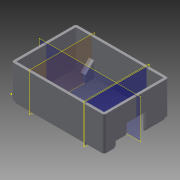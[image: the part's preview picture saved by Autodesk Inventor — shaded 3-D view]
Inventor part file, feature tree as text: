
AUTODESK INVENTOR PART (.ipt)
format: ipt  version: 2015 (Build 190159000, 159)  size: 256,512 bytes
history: native  units: in
note: dims shown in document units (in); Inventor stores cm internally (conversion verified against a paired STEP export)
features: sketch x10, extrude x5, plane x4, fillet x3, rib x3, hole x1, mirror x1
ambient origin geometry x8: Origin, YZ Plane, XZ Plane, XY Plane, X Axis, Y Axis, Z Axis, Center Point
bodies: Solid1 (feature_tree)
feature tree (27):
  extrude  "Extrusion1"  Depth=2.5197in
  extrude  "Extrusion2"  Depth=0.0984in
  fillet  "Fillet1"  Radius=0.0984in
  sketch  "Sketch4"  dims[d7=0.0984in d8=1.2795in d9=0.0in]
  extrude  "Extrusion4"  Depth=1.2795in TaperAngle=0.0deg
  extrude  "Extrusion5"  Depth=0.0787in
  hole  "Hole1"  [1 undecoded]
  extrude  "Extrusion6"  Depth=0.3346in
  fillet  "Fillet2"  [1 undecoded]
  sketch  "Sketch10"  dims[d26=0.3346in]
  plane  "Work Plane1"
  rib  "Rib1"
  plane  "Work Plane2"
  mirror  "Mirror1"
  plane  "Work Plane4"
  rib  "Rib2"
  plane  "Work Plane5"
  rib  "Rib3"
  fillet  "Fillet3"  Radius=0.1969in
  sketch  "Sketch2"  dims[d2=3.622in d3=2.5197in]
  sketch  "Sketch3"  dims[d4=0.0984in d5=0.0984in d6=0.0984in]
  sketch  "Sketch6"  dims[d10=0.0591in d11=0.0in d12=0.0787in]
  sketch  "Sketch8"  dims[d17=0.2362in d18=0.2362in]
  sketch  "Sketch9"  dims[d22=0.1969in d23=0.3346in d24=0.0in d25=0.1969in]
  sketch  "Sketch12"  dims[d27=0.0in]
  sketch  "Sketch14"  dims[d28=0.1969in]
  sketch  "Sketch15"  dims[d29=0.3346in d30=0.0in d31=0.0984in d33=0.0984in d34=0.1969in d35=0.3346in d36=0.0in d37=0.0984in d38=0.0984in d39=0.0394in d40=0.0984in d43=0.0984in d44=0.0in d45=0.2756in d46=0.0in d47=0.1181in d48=0.0984in d49=0.1181in d50=0.0984in d51=0.1181in d52=0.1181in d53=0.315in d54=0.0984in d55=0.315in d56=0.315in d57=0.0984in d58=0.315in d59=0.1181in d60=0.2362in d61=0.1575in d62=0.0787in d63=90.0deg d64=0.1969in d65=0.0in d66=0.7874in d67=0.3543in d68=0.6693in d69=0.4331in d70=0.3937in d71=0.1969in d72=0.0in d73=0.0787in d74=0.6102in d77=0.0394in d78=0.1969in d79=0.0in d80=0.0in d81=0.0394in d82=0.0394in d86=0.6496in d89=0.6102in d90=0.689in d91=0.0394in d92=0.1969in d93=0.0in d94=0.0in d95=0.0394in d96=0.0394in d97=135.0deg d98=45.0deg d99=0.6496in d101=45.0deg d102=0.0394in d103=0.1969in d104=0.0in d105=0.0in d106=0.0394in d107=0.0394in d108=0.6102in d109=0.689in d110=0.0787in]
note: 2 required parameter values undecoded (feature->parameter linkage not recoverable at this tier; creation-order binding heuristic only, values carry confidence <= 0.55)
